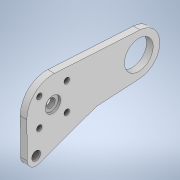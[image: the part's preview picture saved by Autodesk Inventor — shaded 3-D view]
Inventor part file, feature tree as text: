
AUTODESK INVENTOR PART (.ipt)
format: ipt  version: 2020 (Build 240168000, 168)  size: 208,896 bytes
history: native  units: mm
features: extrude x5, sketch x5, projected_geometry x3
ambient origin geometry x8: Origin, YZ Plane, XZ Plane, XY Plane, X Axis, Y Axis, Z Axis, Center Point
bodies: Body1 (feature_tree)
feature tree (13):
  extrude  "Выдавливание4"  Depth=18.6mm
  extrude  "Выдавливание5"  Depth=12.2mm
  extrude  "Выдавливание6"  Depth=9.7mm
  extrude  "Выдавливание7"  Depth=7.1mm
  extrude  "Выдавливание8"  Depth=38.82013mm
  sketch  "Эскиз1"
  sketch  "Эскиз4"
  projected_geometry  "Спроецированная петля3"
  sketch  "Эскиз5"
  sketch  "Эскиз6"
  projected_geometry  "Спроецированная петля4"
  sketch  "Эскиз7"
  projected_geometry  "Спроецированная петля5"
